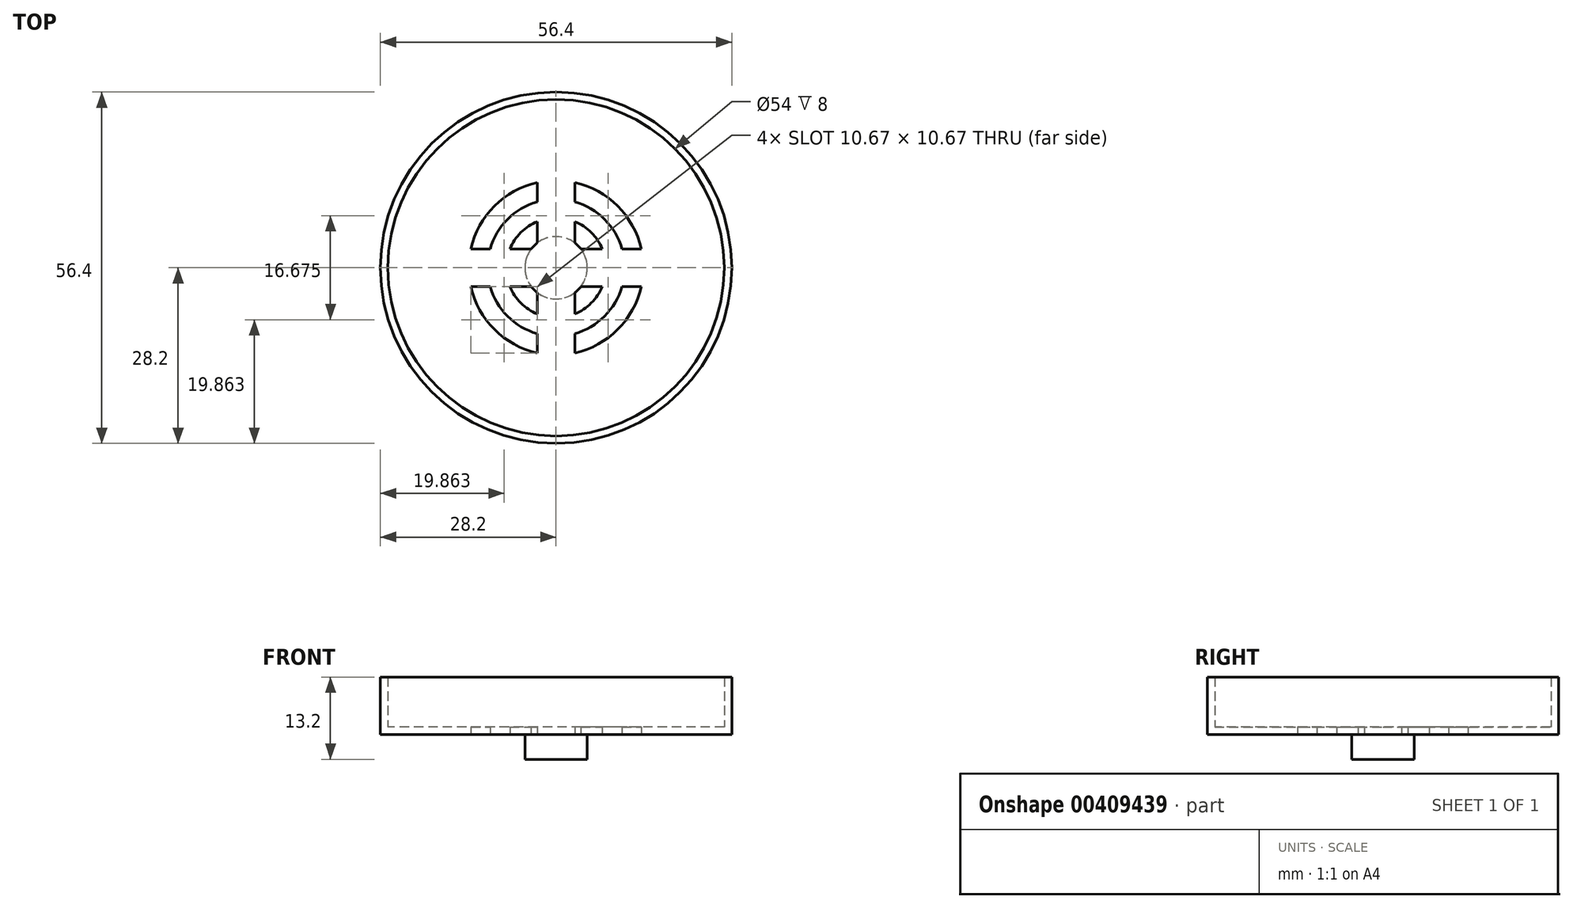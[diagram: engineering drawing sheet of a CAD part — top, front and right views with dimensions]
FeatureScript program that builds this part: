
annotation { "Feature Type Name" : "Feature", "Feature Type Description" : "" }
export const myFeature = defineFeature(function(context is Context, id is Id, definition is map)
    precondition{}
    {
        {
            var Q0;
            Q0=qCreatedBy(makeId("Top.planeOp"),FACE);
            var sketch = newSketch(context, id + "F0", { "sketchPlane" : qUnion([Q0])});
            skCircle(sketch, "E0", {"center": v(0, 0) * mm, "radius": 28.2 * mm});
            skSolve(sketch);
        }
        {
            var Q0;
            Q0 = qSketchRegion(id + "F0", true);
            extrude(context, id + "F1", {"entities" : qUnion([Q0]), "depth" : 9.2 * mm, "offsetDistance" : 25 * mm});
        }
        {
            var Q0;
            Q0=makeQuery(id+"F1.opExtrude","CAP_FACE",FACE,{"disambiguationData":[OSD([sQuery(id+"F0.wireOp",EDGE,"E0")])],"isStart":false});
            shell(context, id + "F2", {"entities" : qUnion([Q0]), "thickness" : 1.2 * mm});
        }
        {
            var Q0;
            Q0=makeQuery(id+"F1.opExtrude","CAP_FACE",FACE,{"disambiguationData":[OSD([sQuery(id+"F0.wireOp",EDGE,"E0")])],"isStart":true});
            var sketch = newSketch(context, id + "F3", { "sketchPlane" : qUnion([Q0])});
            skArc(sketch, "E1", {"start": v(3, -4) * mm, "mid": v(3.54, -3.54) * mm, "end": v(4, -3) * mm});
            skArc(sketch, "E2", {"start": v(3, -7.42) * mm, "mid": v(5.66, -5.66) * mm, "end": v(7.42, -3) * mm});
            skArc(sketch, "E3", {"start": v(3, -10.58) * mm, "mid": v(7.78, -7.78) * mm, "end": v(10.58, -3) * mm});
            skArc(sketch, "E4", {"start": v(3, -13.67) * mm, "mid": v(9.9, -9.9) * mm, "end": v(13.67, -3) * mm});
            skLineSegment(sketch, "E5", {"start": v(0, -22.23) * mm, "end": v(0, 35.27) * mm, "construction": true});
            skLineSegment(sketch, "E6", {"start": v(-33.73, 0) * mm, "end": v(34.87, 0) * mm, "construction": true});
            skLineSegment(sketch, "E7", {"start": v(3, -13.67) * mm, "end": v(3, -10.58) * mm});
            skLineSegment(sketch, "E8", {"start": v(-3, -13.67) * mm, "end": v(-3, -10.58) * mm});
            skArc(sketch, "E9.trimOffspring", {"start": v(-3, 4) * mm, "mid": v(-3.54, 3.54) * mm, "end": v(-4, 3) * mm});
            skArc(sketch, "E10.trimOffspring", {"start": v(-3, 7.42) * mm, "mid": v(-5.66, 5.66) * mm, "end": v(-7.42, 3) * mm});
            skArc(sketch, "E11.trimOffspring", {"start": v(-3, 10.58) * mm, "mid": v(-7.78, 7.78) * mm, "end": v(-10.58, 3) * mm});
            skArc(sketch, "E12.trimOffspring", {"start": v(-3, 13.67) * mm, "mid": v(-9.9, 9.9) * mm, "end": v(-13.67, 3) * mm});
            skPoint(sketch, "E13.orphan", {"position": v(-3, 19) * mm});
            skPoint(sketch, "E14.orphan", {"position": v(3, 19) * mm});
            skLineSegment(sketch, "E15", {"start": v(13.67, -3) * mm, "end": v(10.58, -3) * mm});
            skLineSegment(sketch, "E16", {"start": v(13.67, 3) * mm, "end": v(10.58, 3) * mm});
            skArc(sketch, "E17.trimOffspring", {"start": v(13.67, 3) * mm, "mid": v(9.9, 9.9) * mm, "end": v(3, 13.67) * mm});
            skArc(sketch, "E18.trimOffspring", {"start": v(10.58, 3) * mm, "mid": v(7.78, 7.78) * mm, "end": v(3, 10.58) * mm});
            skArc(sketch, "E19.trimOffspring", {"start": v(7.42, 3) * mm, "mid": v(5.66, 5.66) * mm, "end": v(3, 7.42) * mm});
            skPoint(sketch, "E20.orphan", {"position": v(-24.5, 3) * mm});
            skArc(sketch, "E21.trimOffspring", {"start": v(-13.67, -3) * mm, "mid": v(-9.9, -9.9) * mm, "end": v(-3, -13.67) * mm});
            skArc(sketch, "E22.trimOffspring", {"start": v(-10.58, -3) * mm, "mid": v(-7.78, -7.78) * mm, "end": v(-3, -10.58) * mm});
            skArc(sketch, "E23.trimOffspring", {"start": v(-7.42, -3) * mm, "mid": v(-5.66, -5.66) * mm, "end": v(-3, -7.42) * mm});
            skArc(sketch, "E24.trimOffspring", {"start": v(-4, -3) * mm, "mid": v(-3.54, -3.54) * mm, "end": v(-3, -4) * mm});
            skLineSegment(sketch, "E25.trimOffspring", {"start": v(3, -7.42) * mm, "end": v(3, -4) * mm});
            skLineSegment(sketch, "E26.trimOffspring", {"start": v(7.42, -3) * mm, "end": v(4, -3) * mm});
            skLineSegment(sketch, "E27.trimOffspring", {"start": v(-10.58, -3) * mm, "end": v(-13.67, -3) * mm});
            skLineSegment(sketch, "E28.trimOffspring", {"start": v(-4, -3) * mm, "end": v(-7.42, -3) * mm});
            skLineSegment(sketch, "E29.trimOffspring", {"start": v(-4, 3) * mm, "end": v(-7.42, 3) * mm});
            skLineSegment(sketch, "E30.trimOffspring", {"start": v(3, 4) * mm, "end": v(3, 7.42) * mm});
            skLineSegment(sketch, "E31.trimOffspring", {"start": v(-3, 4) * mm, "end": v(-3, 7.42) * mm});
            skLineSegment(sketch, "E32.trimOffspring", {"start": v(7.42, 3) * mm, "end": v(4, 3) * mm});
            skLineSegment(sketch, "E33.trimOffspring", {"start": v(3, 10.58) * mm, "end": v(3, 13.67) * mm});
            skLineSegment(sketch, "E34.trimOffspring", {"start": v(-3, 10.58) * mm, "end": v(-3, 13.67) * mm});
            skLineSegment(sketch, "E35.trimOffspring", {"start": v(-10.58, 3) * mm, "end": v(-13.67, 3) * mm});
            skArc(sketch, "E36.trimOffspring", {"start": v(4, 3) * mm, "mid": v(3.54, 3.54) * mm, "end": v(3, 4) * mm});
            skLineSegment(sketch, "E37.trimOffspring", {"start": v(-3, -7.42) * mm, "end": v(-3, -4) * mm});
            skSolve(sketch);
        }
        {
            var Q0;
            Q0 = qSketchRegion(id + "F3", true);
            extrude(context, id + "F4", {"entities" : qUnion([Q0]), "operationType" : NewBodyOperationType.REMOVE, "endBound" : BoundingType.THROUGH_ALL, "oppositeDirection" : true, "depth" : 25 * mm, "offsetDistance" : 25 * mm});
        }
        {
            var Q0;
            Q0=makeQuery(id+"F1.opExtrude","CAP_FACE",FACE,{"disambiguationData":[OSD([sQuery(id+"F0.wireOp",EDGE,"E0")])],"isStart":true});
            var sketch = newSketch(context, id + "F5", { "sketchPlane" : qUnion([Q0])});
            skCircle(sketch, "E38", {"center": v(0, 0) * mm, "radius": 5 * mm});
            skSolve(sketch);
        }
        {
            var Q0;
            Q0 = qSketchRegion(id + "F5", true);
            extrude(context, id + "F6", {"entities" : qUnion([Q0]), "operationType" : NewBodyOperationType.ADD, "depth" : 4 * mm, "offsetDistance" : 25 * mm});
        }
    });
